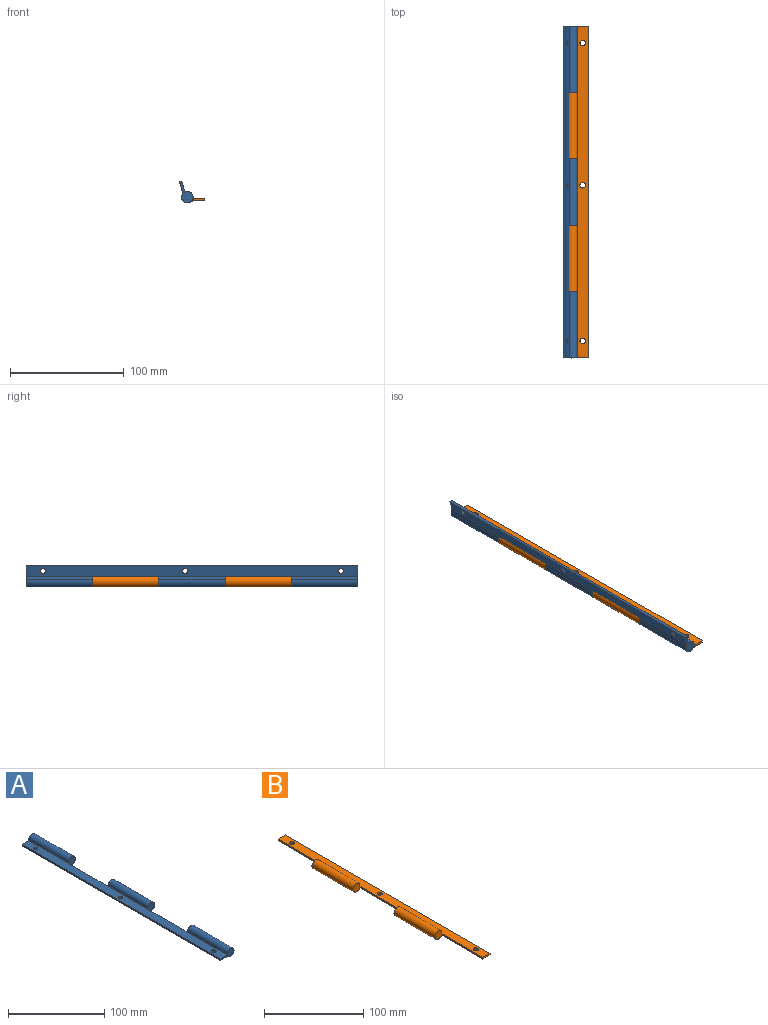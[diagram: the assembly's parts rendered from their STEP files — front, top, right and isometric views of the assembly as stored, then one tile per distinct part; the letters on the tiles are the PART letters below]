
ASSEMBLY  parts=2 mates=1
PART A: 23 faces, bbox 20x292x10 mm
  f0: plane 58.4x1mm, normal (-1,0,0), area 58.4mm2, adj f5,f8,f12,f19
  f1: plane 58.4x1mm, normal (-1,0,0), area 58.4mm2, adj f4,f8,f15,f17
  f2: plane 58.4x2.65mm, normal (-0.47,0,-0.88), area 175.2mm2, adj f4,f10,f15,f17
  f3: plane 58.4x2.65mm, normal (-0.47,0,-0.88), area 175.2mm2, adj f6,f10,f13,f16
  f4: cylinder r=5mm len=58.4mm, axis (0,1,0), area 1519.1mm2, adj f1,f2,f15,f17
  f5: cylinder r=5mm len=58.4mm, axis (0,1,0), area 1519.1mm2, adj f0,f11,f12,f19
  f6: cylinder r=5mm len=58.4mm, axis (0,1,0), area 1519.1mm2, adj f3,f7,f13,f16
  f7: plane 58.4x1mm, normal (-1,0,0), area 58.4mm2, adj f6,f8,f13,f16
  f8: plane 292x10mm, normal (0,0,1), area 2861.1mm2, adj f0,f1,f7,f9,f12,f13,f14,f18
  f9: plane 292x2mm, normal (-1,0,0), area 584mm2, adj f8,f10,f12,f13
  f10: plane 292x10mm, normal (0,0,-1), area 2861.1mm2, adj f2,f3,f9,f11,f12,f13,f14,f18
  f11: plane 58.4x2.65mm, normal (-0.47,0,-0.88), area 175.2mm2, adj f5,f10,f12,f19
  f12: plane 20x10mm, normal (0,-1,0), area 100mm2, adj f0,f5,f8,f9,f10,f11
  f13: plane 20x10mm, normal (0,1,0), area 100mm2, adj f3,f6,f7,f8,f9,f10
  f14: plane 58.4x2mm, normal (1,0,0), area 116.8mm2, adj f8,f10,f15,f16
  f15: plane 10x10mm, normal (0,1,0), area 80mm2, adj f1,f2,f4,f14
  f16: plane 10x10mm, normal (0,-1,0), area 80mm2, adj f3,f6,f7,f14
  f17: plane 10x10mm, normal (0,-1,0), area 80mm2, adj f1,f2,f4,f18
  f18: plane 58.4x2mm, normal (1,0,0), area 116.8mm2, adj f8,f10,f17,f19
  f19: plane 10x10mm, normal (0,1,0), area 80mm2, adj f0,f5,f11,f18
  f20: cylinder r=2.5mm len=5mm, axis (0,0,1), area 31.4mm2, adj f8,f10
  f21: cylinder r=2.5mm len=5mm, axis (0,0,1), area 31.4mm2, adj f8,f10
  f22: cylinder r=2.5mm len=5mm, axis (0,0,1), area 31.4mm2, adj f8,f10
PART B: 21 faces, bbox 20x292x10 mm
  f0: plane 58.4x1mm, normal (1,0,0), area 58.4mm2, adj f5,f8,f12,f16
  f1: plane 58.4x1mm, normal (1,0,0), area 58.4mm2, adj f4,f8,f13,f14
  f2: plane 58.4x2.65mm, normal (0.47,0,-0.88), area 175.2mm2, adj f4,f10,f13,f14
  f3: plane 58.4x2.65mm, normal (0.47,0,-0.88), area 175.2mm2, adj f5,f10,f12,f16
  f4: cylinder r=5mm len=58.4mm, axis (0,1,0), area 1519.1mm2, adj f1,f2,f13,f14
  f5: cylinder r=5mm len=58.4mm, axis (0,1,0), area 1519.1mm2, adj f0,f3,f12,f16
  f6: plane 10x2mm, normal (0,-1,0), area 20mm2, adj f8,f9,f10,f15
  f7: plane 10x2mm, normal (0,1,0), area 20mm2, adj f8,f9,f10,f17
  f8: plane 292x10mm, normal (0,0,1), area 2861.1mm2, adj f0,f1,f6,f7,f9,f11,f15,f17
  f9: plane 292x2mm, normal (1,0,0), area 584mm2, adj f6,f7,f8,f10
  f10: plane 292x10mm, normal (0,0,-1), area 2861.1mm2, adj f2,f3,f6,f7,f9,f11,f15,f17
  f11: plane 58.4x2mm, normal (-1,0,0), area 116.8mm2, adj f8,f10,f12,f13
  f12: plane 10x10mm, normal (0,-1,0), area 80mm2, adj f0,f3,f5,f11
  f13: plane 10x10mm, normal (0,1,0), area 80mm2, adj f1,f2,f4,f11
  f14: plane 10x10mm, normal (0,-1,0), area 80mm2, adj f1,f2,f4,f15
  f15: plane 58.4x2mm, normal (-1,0,0), area 116.8mm2, adj f6,f8,f10,f14
  f16: plane 10x10mm, normal (0,1,0), area 80mm2, adj f0,f3,f5,f17
  f17: plane 58.4x2mm, normal (-1,0,0), area 116.8mm2, adj f7,f8,f10,f16
  f18: cylinder r=2.5mm len=5mm, axis (0,0,1), area 31.4mm2, adj f8,f10
  f19: cylinder r=2.5mm len=5mm, axis (0,0,1), area 31.4mm2, adj f8,f10
  f20: cylinder r=2.5mm len=5mm, axis (0,0,1), area 31.4mm2, adj f8,f10
PLACE A rot(axis=(0,1,0),74.7deg) t=(-71.58,88.49,-20.18)mm
PLACE B rot(axis=(0,-1,0),0.3deg) t=(-364.3,88.49,-27.03)mm
MATE revolute B.f4 <-> A.f4  axis (0,1,0) through (-69.3,30.09,-24.74)mm
